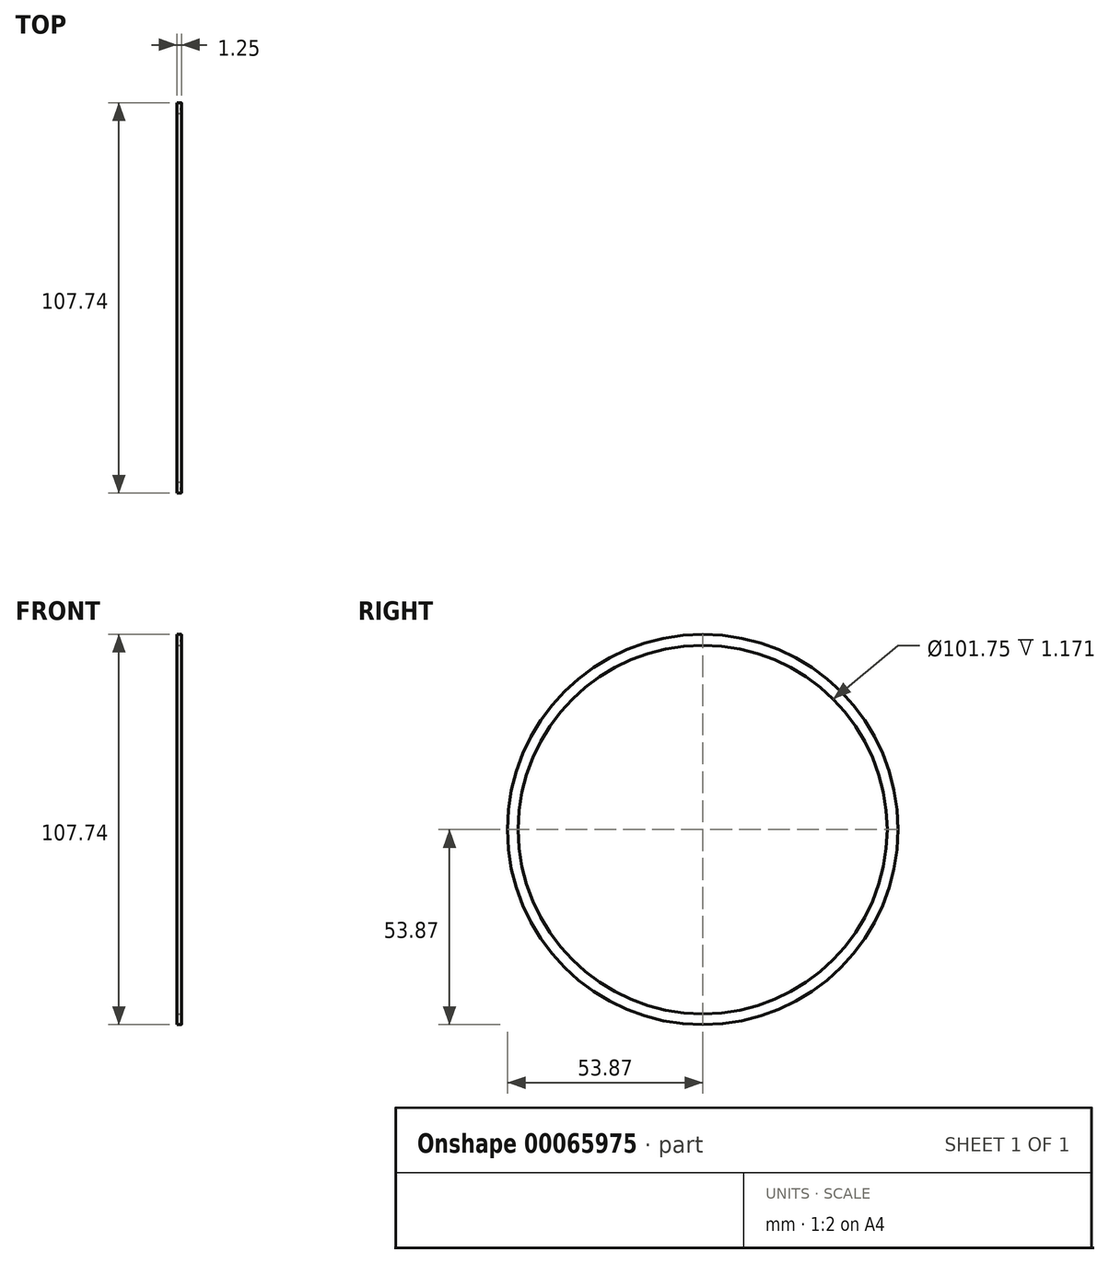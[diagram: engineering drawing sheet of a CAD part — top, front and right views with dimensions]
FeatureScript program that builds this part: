
annotation { "Feature Type Name" : "Feature", "Feature Type Description" : "" }
export const myFeature = defineFeature(function(context is Context, id is Id, definition is map)
    precondition{}
    {
        {
            var Q0;
            Q0=qCreatedBy(makeId("Front.planeOp"),FACE);
            var sketch = newSketch(context, id + "F0", { "sketchPlane" : qUnion([Q0])});
            skLineSegment(sketch, "E0.bottom", {"start": v(-0.1, 53.87) * mm, "end": v(-1.28, 53.87) * mm});
            skLineSegment(sketch, "E0.top", {"start": v(-0.1, 50.88) * mm, "end": v(-1.28, 50.88) * mm});
            skLineSegment(sketch, "E0.right", {"start": v(-1.28, 53.87) * mm, "end": v(-1.28, 50.88) * mm});
            skLineSegment(sketch, "E1", {"start": v(0, 0) * mm, "end": v(-6.16, 0) * mm, "construction": true});
            skArc(sketch, "E2", {"start": v(-0.03, 53.77) * mm, "mid": v(-0.26, 52.37) * mm, "end": v(-0.03, 50.98) * mm});
            skPoint(sketch, "E3.visualSharp", {"position": v(0, 53.87) * mm});
            skArc(sketch, "E3.filletArc", {"start": v(-0.03, 53.77) * mm, "mid": v(-0.05, 53.84) * mm, "end": v(-0.1, 53.87) * mm});
            skPoint(sketch, "E4.visualSharp", {"position": v(0, 50.88) * mm});
            skArc(sketch, "E4.filletArc", {"start": v(-0.1, 50.88) * mm, "mid": v(-0.05, 50.9) * mm, "end": v(-0.03, 50.98) * mm});
            skLineSegment(sketch, "E5", {"start": v(0, 50.88) * mm, "end": v(0, 0) * mm, "construction": true});
            skSolve(sketch);
        }
        {
            var Q0;
            Q0=makeQuery(id+"F0.imprint","IMPRINT",FACE,{"disambiguationData":[TD([[makeQuery(id+"F0.imprint","IMPRINT",EDGE,{"derivedFrom":sQuery(id+"F0.wireOp",EDGE,"E0.bottom")}),1.0]])]});
            var Q1;
            Q1=sQuery(id+"F0.wireOp",EDGE,"E1");
            revolve(context, id + "F1", {"entities" : qUnion([Q0]), "axis" : qUnion([Q1]), "revolveType" : RevolveType.FULL});
        }
    });
